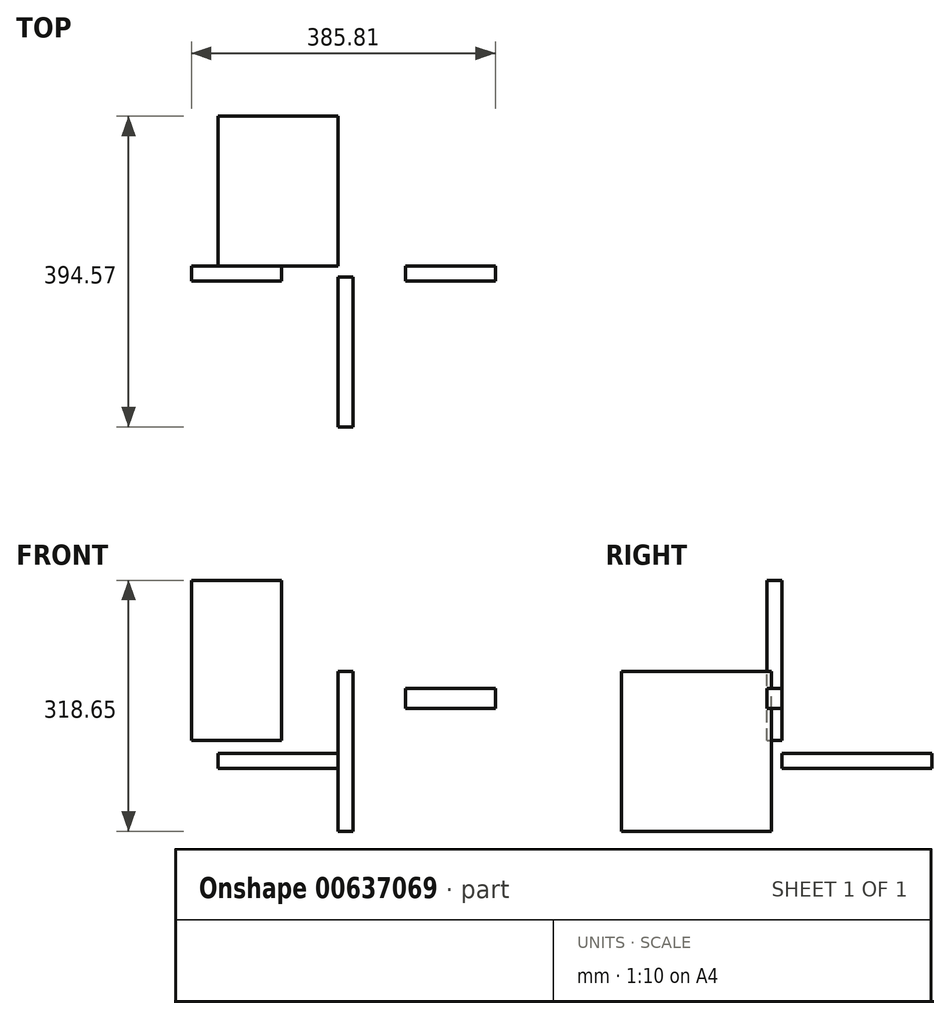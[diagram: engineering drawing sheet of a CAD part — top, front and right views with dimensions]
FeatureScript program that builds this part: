
annotation { "Feature Type Name" : "Feature", "Feature Type Description" : "" }
export const myFeature = defineFeature(function(context is Context, id is Id, definition is map)
    precondition{}
    {
        {
            var Q0;
            Q0=qCreatedBy(makeId("Top.planeOp"),FACE);
            var sketch = newSketch(context, id + "F0", { "sketchPlane" : qUnion([Q0])});
            skLineSegment(sketch, "E0.bottom", {"start": v(0, 0) * mm, "end": v(-152.4, 0) * mm});
            skLineSegment(sketch, "E0.top", {"start": v(0, 190.5) * mm, "end": v(-152.4, 190.5) * mm});
            skLineSegment(sketch, "E0.left", {"start": v(0, 0) * mm, "end": v(0, 190.5) * mm});
            skLineSegment(sketch, "E0.right", {"start": v(-152.4, 0) * mm, "end": v(-152.4, 190.5) * mm});
            skSolve(sketch);
        }
        {
            var Q0;
            Q0 = qSketchRegion(id + "F0", true);
            extrude(context, id + "F1", {"entities" : qUnion([Q0]), "depth" : 19.05 * mm, "offsetDistance" : 25.4 * mm});
        }
        {
            var Q0;
            Q0=qCreatedBy(makeId("Front.planeOp"),FACE);
            var sketch = newSketch(context, id + "F2", { "sketchPlane" : qUnion([Q0])});
            skLineSegment(sketch, "E1.bottom", {"start": v(-71.57, 35.5) * mm, "end": v(-185.87, 35.5) * mm});
            skLineSegment(sketch, "E1.top", {"start": v(-71.57, 238.7) * mm, "end": v(-185.87, 238.7) * mm});
            skLineSegment(sketch, "E1.left", {"start": v(-71.57, 35.5) * mm, "end": v(-71.57, 238.7) * mm});
            skLineSegment(sketch, "E1.right", {"start": v(-185.87, 35.5) * mm, "end": v(-185.87, 238.7) * mm});
            skSolve(sketch);
        }
        {
            var Q0;
            Q0 = qSketchRegion(id + "F2", true);
            extrude(context, id + "F3", {"entities" : qUnion([Q0]), "depth" : 19.05 * mm, "offsetDistance" : 25.4 * mm});
        }
        {
            var Q0;
            Q0=qCreatedBy(makeId("Right.planeOp"),FACE);
            var sketch = newSketch(context, id + "F4", { "sketchPlane" : qUnion([Q0])});
            skLineSegment(sketch, "E2.bottom", {"start": v(-13.57, -79.95) * mm, "end": v(-204.07, -79.95) * mm});
            skLineSegment(sketch, "E2.top", {"start": v(-13.57, 123.25) * mm, "end": v(-204.07, 123.25) * mm});
            skLineSegment(sketch, "E2.left", {"start": v(-13.57, -79.95) * mm, "end": v(-13.57, 123.25) * mm});
            skLineSegment(sketch, "E2.right", {"start": v(-204.07, -79.95) * mm, "end": v(-204.07, 123.25) * mm});
            skSolve(sketch);
        }
        {
            var Q0;
            Q0 = qSketchRegion(id + "F4", true);
            extrude(context, id + "F5", {"entities" : qUnion([Q0]), "depth" : 19.05 * mm, "offsetDistance" : 25.4 * mm});
        }
        {
            var Q0;
            Q0=qCreatedBy(makeId("Front.planeOp"),FACE);
            var sketch = newSketch(context, id + "F6", { "sketchPlane" : qUnion([Q0])});
            skLineSegment(sketch, "E3.bottom", {"start": v(85.64, 76.35) * mm, "end": v(199.94, 76.35) * mm});
            skLineSegment(sketch, "E3.top", {"start": v(85.64, 101.75) * mm, "end": v(199.94, 101.75) * mm});
            skLineSegment(sketch, "E3.left", {"start": v(85.64, 76.35) * mm, "end": v(85.64, 101.75) * mm});
            skLineSegment(sketch, "E3.right", {"start": v(199.94, 76.35) * mm, "end": v(199.94, 101.75) * mm});
            skSolve(sketch);
        }
        {
            var Q0;
            Q0 = qSketchRegion(id + "F6", true);
            extrude(context, id + "F7", {"entities" : qUnion([Q0]), "depth" : 19.05 * mm, "offsetDistance" : 25.4 * mm});
        }
    });
